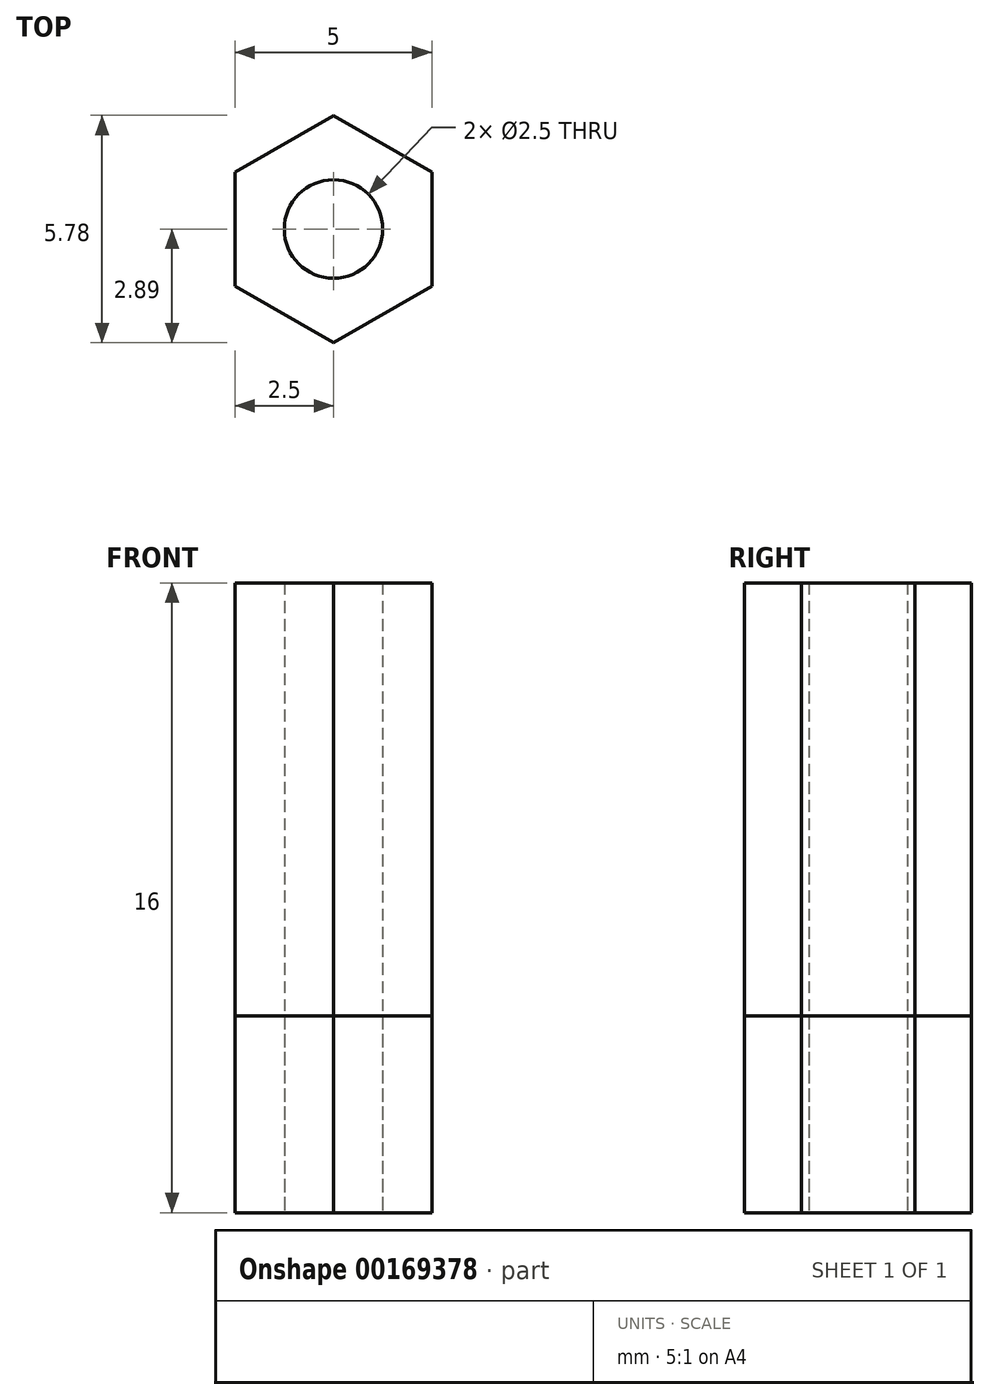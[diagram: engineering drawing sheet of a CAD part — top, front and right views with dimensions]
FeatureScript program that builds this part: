
annotation { "Feature Type Name" : "Feature", "Feature Type Description" : "" }
export const myFeature = defineFeature(function(context is Context, id is Id, definition is map)
    precondition{}
    {
        {
            var Q0;
            Q0=qCreatedBy(makeId("Top.planeOp"),FACE);
            var sketch = newSketch(context, id + "F0", { "sketchPlane" : qUnion([Q0])});
            skCircle(sketch, "E0.cCircle", {"center": v(0, 0) * mm, "radius": 2.5 * mm, "construction": true});
            skLineSegment(sketch, "E0.0", {"start": v(-2.5, -1.44) * mm, "end": v(-2.5, 1.44) * mm});
            skLineSegment(sketch, "E0.1", {"start": v(-2.5, 1.44) * mm, "end": v(0, 2.89) * mm});
            skLineSegment(sketch, "E0.2", {"start": v(0, 2.89) * mm, "end": v(2.5, 1.44) * mm});
            skLineSegment(sketch, "E0.3", {"start": v(2.5, 1.44) * mm, "end": v(2.5, -1.44) * mm});
            skLineSegment(sketch, "E0.4", {"start": v(2.5, -1.44) * mm, "end": v(0, -2.89) * mm});
            skLineSegment(sketch, "E0.5", {"start": v(0, -2.89) * mm, "end": v(-2.5, -1.44) * mm});
            skPoint(sketch, "E0.0.midPoint", {"position": v(-2.5, 0) * mm});
            skCircle(sketch, "E1", {"center": v(0, 0) * mm, "radius": 1.25 * mm});
            skSolve(sketch);
        }
        {
            var Q0;
            Q0 = qSketchRegion(id + "F0", true);
            extrude(context, id + "F1", {"entities" : qUnion([Q0]), "depth" : 5 * mm});
        }
        {
            var Q0;
            Q0 = qSketchRegion(id + "F0", true);
            extrude(context, id + "F2", {"entities" : qUnion([Q0]), "depth" : 16 * mm});
        }
    });
